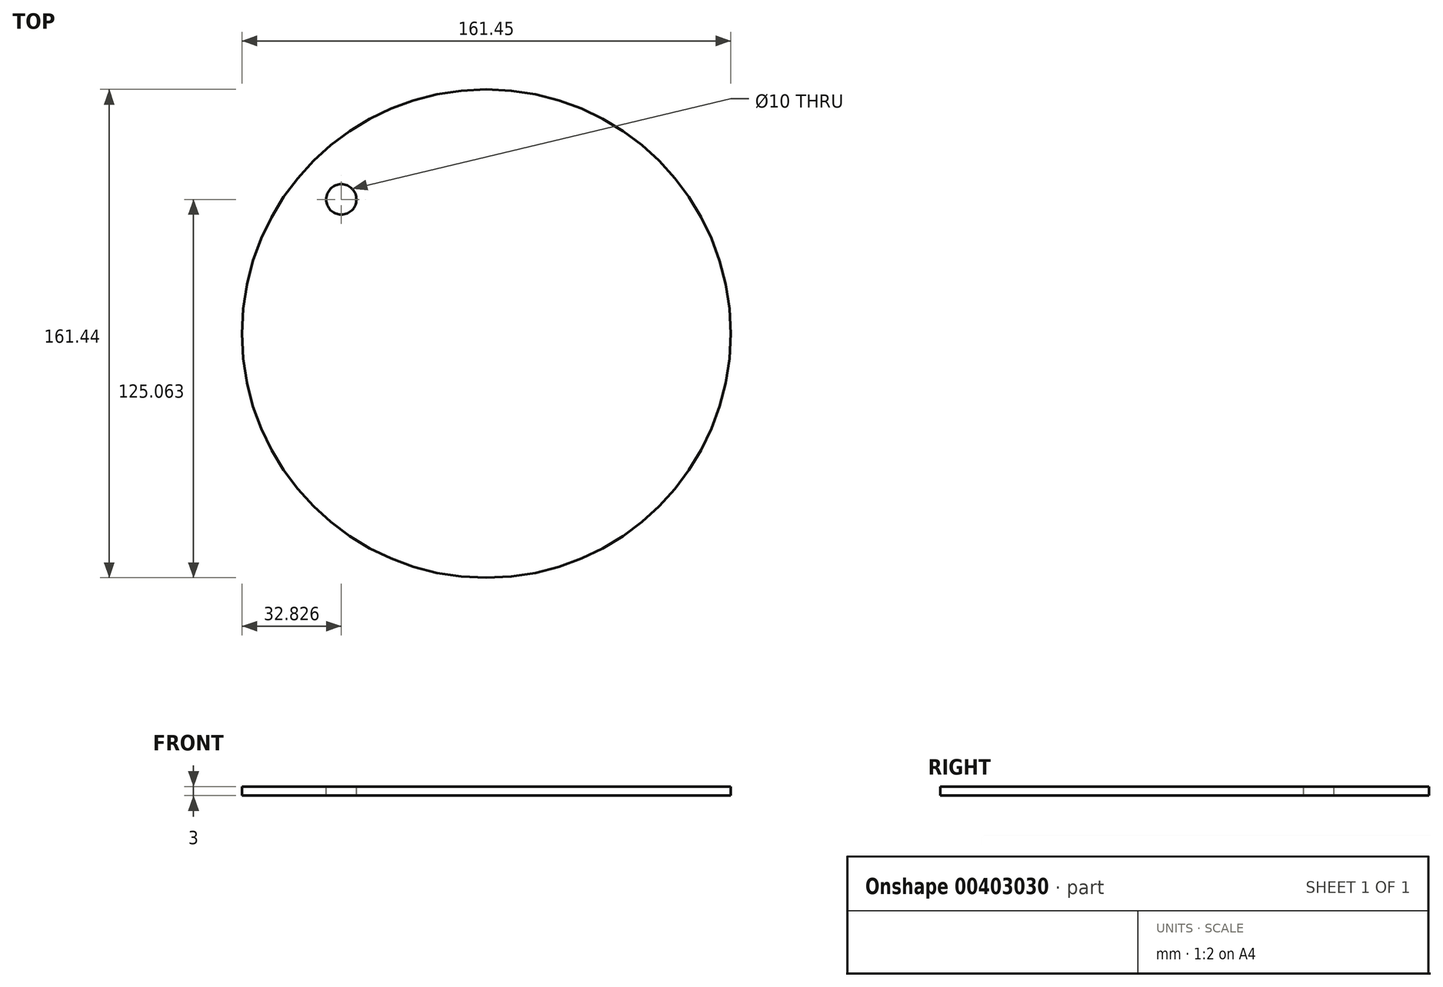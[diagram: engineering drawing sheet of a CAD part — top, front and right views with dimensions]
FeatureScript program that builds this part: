
annotation { "Feature Type Name" : "Feature", "Feature Type Description" : "" }
export const myFeature = defineFeature(function(context is Context, id is Id, definition is map)
    precondition{}
    {
        {
            var Q0;
            Q0=qCreatedBy(makeId("Top.planeOp"),FACE);
            var sketch = newSketch(context, id + "F0", { "sketchPlane" : qUnion([Q0])});
            skCircle(sketch, "E0", {"center": v(-61.54, 32.26) * mm, "radius": 80.72 * mm});
            skSolve(sketch);
        }
        {
            var Q0;
            Q0=makeQuery(id+"F0.imprint","IMPRINT",FACE,{"disambiguationData":[TD([[makeQuery(id+"F0.imprint","IMPRINT",EDGE,{"derivedFrom":sQuery(id+"F0.wireOp",EDGE,"E0")}),1.0]])]});
            extrude(context, id + "F1", {"entities" : qUnion([Q0]), "depth" : 3 * mm});
        }
        {
            var Q0;
            Q0=makeQuery(id+"F1.opExtrude","CAP_FACE",FACE,{"disambiguationData":[OSD([sQuery(id+"F0.wireOp",EDGE,"E0")])],"isStart":false});
            var sketch = newSketch(context, id + "F2", { "sketchPlane" : qUnion([Q0])});
            skCircle(sketch, "E1", {"center": v(-128.83, 47.31) * mm, "radius": 3 * mm});
            skSolve(sketch);
        }
        {
            var Q0;
            Q0=makeQuery(id+"F2.imprint","IMPRINT",FACE,{"disambiguationData":[TD([[makeQuery(id+"F2.imprint","IMPRINT",EDGE,{"derivedFrom":sQuery(id+"F2.wireOp",EDGE,"E1")}),1.0]])]});
            extrude(context, id + "F3", {"entities" : qUnion([Q0]), "operationType" : NewBodyOperationType.ADD, "oppositeDirection" : true, "depth" : 3 * mm});
        }
        {
            var Q0;
            Q0=makeQuery(id+"F1.opExtrude","CAP_FACE",FACE,{"disambiguationData":[OSD([sQuery(id+"F0.wireOp",EDGE,"E0")])],"isStart":false});
            var sketch = newSketch(context, id + "F4", { "sketchPlane" : qUnion([Q0])});
            skPoint(sketch, "E2", {"position": v(-109.43, 76.6) * mm});
            skPoint(sketch, "E3.1.0", {"position": v(-99.52, 85.34) * mm});
            skPoint(sketch, "E3.2.0", {"position": v(-88.05, 91.9) * mm});
            skPoint(sketch, "E3.3.0", {"position": v(-75.5, 96.02) * mm});
            skPoint(sketch, "E3.4.0", {"position": v(-62.36, 97.53) * mm});
            skPoint(sketch, "E3.5.0", {"position": v(-49.2, 96.36) * mm});
            skPoint(sketch, "E3.6.0", {"position": v(-36.54, 92.56) * mm});
            skPoint(sketch, "E3.7.0", {"position": v(-24.9, 86.29) * mm});
            skPoint(sketch, "E3.8.0", {"position": v(-14.77, 77.8) * mm});
            skPoint(sketch, "E3.9.0", {"position": v(-6.56, 67.45) * mm});
            skPoint(sketch, "E3.10.0", {"position": v(-0.6, 55.65) * mm});
            skPoint(sketch, "E3.11.0", {"position": v(2.87, 42.9) * mm});
            skPoint(sketch, "E3.12.0", {"position": v(3.69, 29.7) * mm});
            skPoint(sketch, "E3.13.0", {"position": v(1.84, 16.62) * mm});
            skPoint(sketch, "E3.14.0", {"position": v(-2.61, 4.18) * mm});
            skPoint(sketch, "E3.15.0", {"position": v(-9.48, -7.12) * mm});
            skPoint(sketch, "E3.16.0", {"position": v(-18.47, -16.8) * mm});
            skPoint(sketch, "E3.17.0", {"position": v(-29.24, -24.47) * mm});
            skPoint(sketch, "E3.18.0", {"position": v(-41.33, -29.8) * mm});
            skPoint(sketch, "E3.19.0", {"position": v(-54.24, -32.6) * mm});
            skPoint(sketch, "E3.20.0", {"position": v(-67.46, -32.75) * mm});
            skPoint(sketch, "E3.21.0", {"position": v(-80.43, -30.22) * mm});
            skPoint(sketch, "E3.22.0", {"position": v(-92.63, -25.13) * mm});
            skPoint(sketch, "E3.23.0", {"position": v(-103.55, -17.7) * mm});
            skPoint(sketch, "E3.24.0", {"position": v(-112.75, -8.2) * mm});
            skPoint(sketch, "E3.25.0", {"position": v(-119.85, 2.94) * mm});
            skPoint(sketch, "E3.26.0", {"position": v(-124.56, 15.29) * mm});
            skPoint(sketch, "E3.27.0", {"position": v(-126.7, 28.33) * mm});
            skPoint(sketch, "E3.28.0", {"position": v(-126.15, 41.54) * mm});
            skPoint(sketch, "E3.29.0", {"position": v(-122.95, 54.36) * mm});
            skPoint(sketch, "E3.center", {"position": v(-61.54, 32.26) * mm});
            skLineSegment(sketch, "E3.anchor1", {"start": v(-61.54, 32.26) * mm, "end": v(-109.43, 76.6) * mm, "construction": true});
            skLineSegment(sketch, "E3.anchor2", {"start": v(-61.54, 32.26) * mm, "end": v(-122.95, 54.36) * mm, "construction": true});
            skSolve(sketch);
        }
        {
            var Q0;
            Q0=sQuery(id+"F4.wireOp",VERTEX,"E2");
            var Q1;
            Q1=makeQuery(id+"F1.opExtrude","SWEPT_BODY",BODY,{"disambiguationData":[OSD([sQuery(id+"F0.wireOp",EDGE,"E0")])]});
            hole(context, id + "F5", {"style" : HoleStyle.SIMPLE, "endStyle" : HoleEndStyle.THROUGH, "holeDiameter" : 10 * mm, "isTappedThrough" : true, "tappedDepth" : 12 * mm, "tapClearance" : 3, "locations" : qUnion([Q0]), "scope" : qUnion([Q1])});
        }
    });
